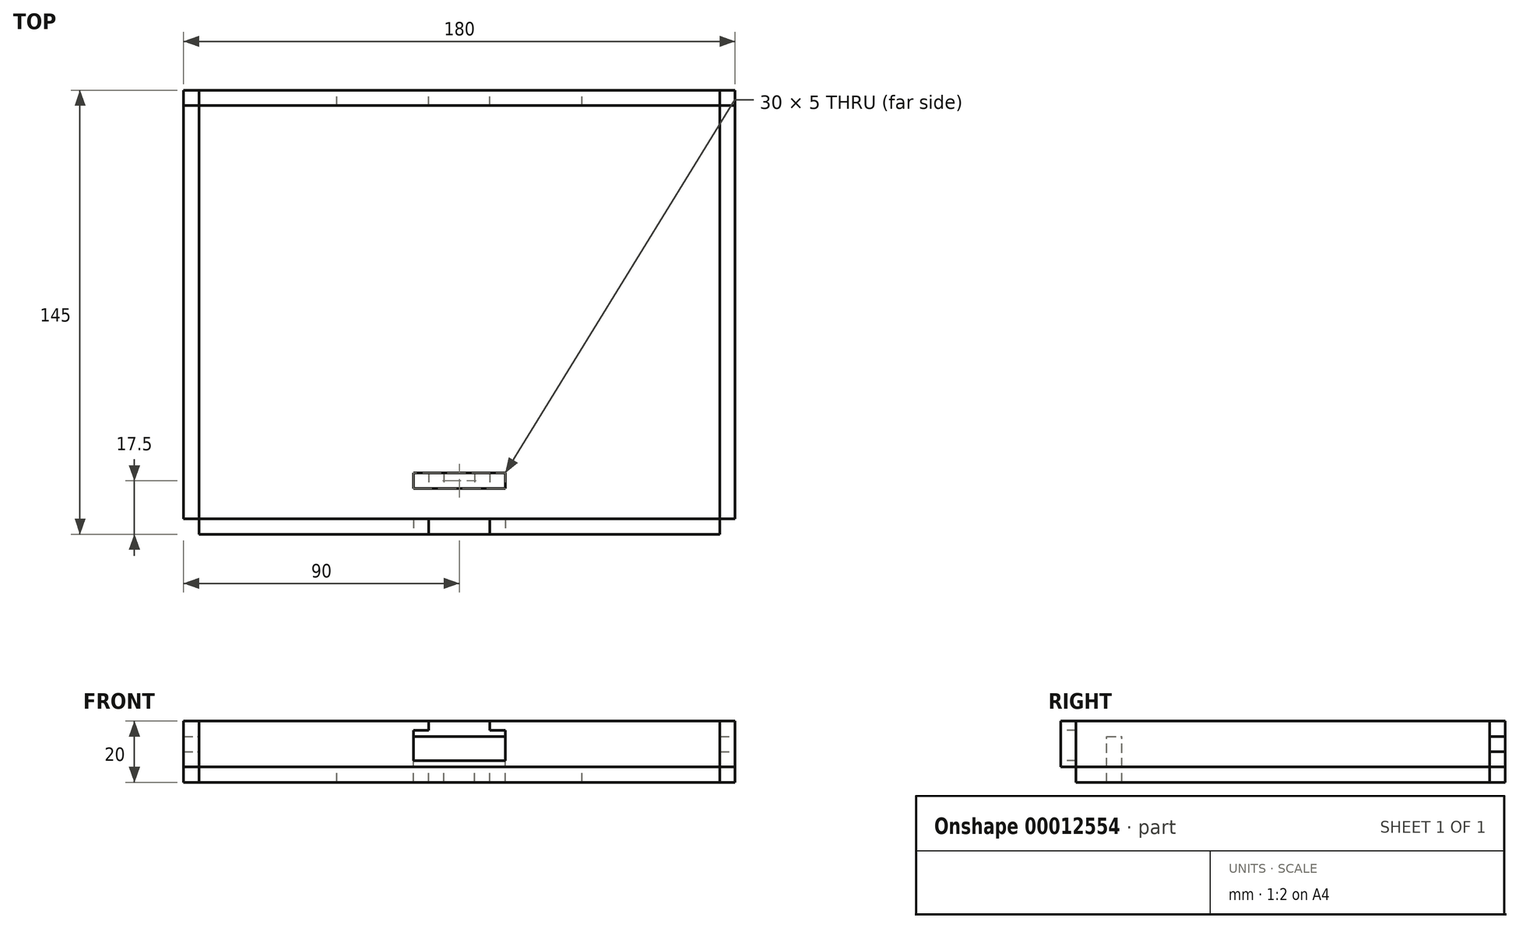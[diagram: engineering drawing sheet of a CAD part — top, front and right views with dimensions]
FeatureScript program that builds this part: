
annotation { "Feature Type Name" : "Feature", "Feature Type Description" : "" }
export const myFeature = defineFeature(function(context is Context, id is Id, definition is map)
    precondition{}
    {
        {
            var Q0;
            Q0=qCreatedBy(makeId("Top.planeOp"),FACE);
            var sketch = newSketch(context, id + "F0", { "sketchPlane" : qUnion([Q0])});
            skLineSegment(sketch, "E0.bottom", {"start": v(0, 0) * mm, "end": v(-180, 0) * mm});
            skLineSegment(sketch, "E0.top", {"start": v(0, 145) * mm, "end": v(-180, 145) * mm});
            skLineSegment(sketch, "E0.left", {"start": v(0, 0) * mm, "end": v(0, 145) * mm});
            skLineSegment(sketch, "E0.right", {"start": v(-180, 0) * mm, "end": v(-180, 145) * mm});
            skSolve(sketch);
        }
        {
            var Q0;
            Q0 = qSketchRegion(id + "F0", true);
            extrude(context, id + "F1", {"entities" : qUnion([Q0]), "depth" : 5 * mm});
        }
        {
            var Q0;
            Q0=makeQuery(id+"F1.opExtrude","SWEPT_FACE",FACE,{"disambiguationData":[OSD([sQuery(id+"F0.wireOp",EDGE,"E0.bottom")])]});
            var sketch = newSketch(context, id + "F2", { "sketchPlane" : qUnion([Q0])});
            skLineSegment(sketch, "E1.bottom", {"start": v(-180, 0) * mm, "end": v(0, 0) * mm});
            skLineSegment(sketch, "E1.top", {"start": v(-180, 20) * mm, "end": v(0, 20) * mm});
            skLineSegment(sketch, "E1.left", {"start": v(-180, 0) * mm, "end": v(-180, 20) * mm});
            skLineSegment(sketch, "E1.right", {"start": v(0, 0) * mm, "end": v(0, 20) * mm});
            skSolve(sketch);
        }
        {
            var Q0;
            Q0 = qSketchRegion(id + "F2", true);
            extrude(context, id + "F3", {"entities" : qUnion([Q0]), "oppositeDirection" : true, "depth" : 5 * mm});
        }
        {
            var Q0;
            Q0=makeQuery(id+"F1.opExtrude","SWEPT_FACE",FACE,{"disambiguationData":[OSD([sQuery(id+"F0.wireOp",EDGE,"E0.right")])]});
            var sketch = newSketch(context, id + "F4", { "sketchPlane" : qUnion([Q0])});
            skLineSegment(sketch, "E2.bottom", {"start": v(-145, 0) * mm, "end": v(0, 0) * mm});
            skLineSegment(sketch, "E2.top", {"start": v(-145, 20) * mm, "end": v(0, 20) * mm});
            skLineSegment(sketch, "E2.left", {"start": v(-145, 0) * mm, "end": v(-145, 20) * mm});
            skLineSegment(sketch, "E2.right", {"start": v(0, 0) * mm, "end": v(0, 20) * mm});
            skSolve(sketch);
        }
        {
            var Q0;
            Q0 = qSketchRegion(id + "F4", true);
            extrude(context, id + "F5", {"entities" : qUnion([Q0]), "oppositeDirection" : true, "depth" : 5 * mm});
        }
        {
            var Q0;
            Q0=makeQuery(id+"F1.opExtrude","SWEPT_FACE",FACE,{"disambiguationData":[OSD([sQuery(id+"F0.wireOp",EDGE,"E0.left")])]});
            var sketch = newSketch(context, id + "F6", { "sketchPlane" : qUnion([Q0])});
            skLineSegment(sketch, "E3.bottom", {"start": v(0, 0) * mm, "end": v(145, 0) * mm});
            skLineSegment(sketch, "E3.top", {"start": v(0, 20) * mm, "end": v(145, 20) * mm});
            skLineSegment(sketch, "E3.left", {"start": v(0, 0) * mm, "end": v(0, 20) * mm});
            skLineSegment(sketch, "E3.right", {"start": v(145, 0) * mm, "end": v(145, 20) * mm});
            skSolve(sketch);
        }
        {
            var Q0;
            Q0 = qSketchRegion(id + "F6", true);
            extrude(context, id + "F7", {"entities" : qUnion([Q0]), "oppositeDirection" : true, "depth" : 5 * mm});
        }
        {
            var Q0;
            Q0=makeQuery(id+"F5.opExtrude","CAP_FACE",FACE,{"disambiguationData":[OSD([sQuery(id+"F4.wireOp",EDGE,"E2.bottom"),sQuery(id+"F4.wireOp",EDGE,"E2.top"),sQuery(id+"F4.wireOp",EDGE,"E2.left"),sQuery(id+"F4.wireOp",EDGE,"E2.right")])],"isStart":true});
            var sketch = newSketch(context, id + "F8", { "sketchPlane" : qUnion([Q0])});
            skLineSegment(sketch, "E4.bottom", {"start": v(0, 5) * mm, "end": v(-5, 5) * mm});
            skLineSegment(sketch, "E4.top", {"start": v(0, 0) * mm, "end": v(-5, 0) * mm});
            skLineSegment(sketch, "E4.left", {"start": v(0, 5) * mm, "end": v(0, 0) * mm});
            skLineSegment(sketch, "E4.right", {"start": v(-5, 5) * mm, "end": v(-5, 0) * mm});
            skLineSegment(sketch, "E5.bottom", {"start": v(0, 10) * mm, "end": v(-5, 10) * mm});
            skLineSegment(sketch, "E5.top", {"start": v(0, 15) * mm, "end": v(-5, 15) * mm});
            skLineSegment(sketch, "E5.left", {"start": v(0, 10) * mm, "end": v(0, 15) * mm});
            skLineSegment(sketch, "E5.right", {"start": v(-5, 10) * mm, "end": v(-5, 15) * mm});
            skLineSegment(sketch, "E6.bottom", {"start": v(-30, 0) * mm, "end": v(-55, 0) * mm});
            skLineSegment(sketch, "E6.top", {"start": v(-30, 5) * mm, "end": v(-55, 5) * mm});
            skLineSegment(sketch, "E6.left", {"start": v(-30, 0) * mm, "end": v(-30, 5) * mm});
            skLineSegment(sketch, "E6.right", {"start": v(-55, 0) * mm, "end": v(-55, 5) * mm});
            skLineSegment(sketch, "E7.bottom", {"start": v(-85, 0) * mm, "end": v(-115, 0) * mm});
            skLineSegment(sketch, "E7.top", {"start": v(-85, 5) * mm, "end": v(-115, 5) * mm});
            skLineSegment(sketch, "E7.left", {"start": v(-85, 0) * mm, "end": v(-85, 5) * mm});
            skLineSegment(sketch, "E7.right", {"start": v(-115, 0) * mm, "end": v(-115, 5) * mm});
            skLineSegment(sketch, "E8.bottom", {"start": v(-145, 0) * mm, "end": v(-140, 0) * mm});
            skLineSegment(sketch, "E8.top", {"start": v(-145, 5) * mm, "end": v(-140, 5) * mm});
            skLineSegment(sketch, "E8.left", {"start": v(-145, 0) * mm, "end": v(-145, 5) * mm});
            skLineSegment(sketch, "E8.right", {"start": v(-140, 0) * mm, "end": v(-140, 5) * mm});
            skLineSegment(sketch, "E9.bottom", {"start": v(-145, 10) * mm, "end": v(-140, 10) * mm});
            skLineSegment(sketch, "E9.top", {"start": v(-145, 15) * mm, "end": v(-140, 15) * mm});
            skLineSegment(sketch, "E9.left", {"start": v(-145, 10) * mm, "end": v(-145, 15) * mm});
            skLineSegment(sketch, "E9.right", {"start": v(-140, 10) * mm, "end": v(-140, 15) * mm});
            skSolve(sketch);
        }
        {
            var Q0;
            Q0 = qSketchRegion(id + "F8", true);
            extrude(context, id + "F9", {"entities" : qUnion([Q0]), "operationType" : NewBodyOperationType.REMOVE, "oppositeDirection" : true, "depth" : 5 * mm});
        }
        {
            var Q0;
            Q0=makeQuery(id+"F1.opExtrude","CAP_FACE",FACE,{"disambiguationData":[OSD([sQuery(id+"F0.wireOp",EDGE,"E0.bottom"),sQuery(id+"F0.wireOp",EDGE,"E0.top"),sQuery(id+"F0.wireOp",EDGE,"E0.left"),sQuery(id+"F0.wireOp",EDGE,"E0.right")])],"isStart":false});
            var sketch = newSketch(context, id + "F10", { "sketchPlane" : qUnion([Q0])});
            skLineSegment(sketch, "E10.bottom", {"start": v(-180, 0) * mm, "end": v(-160, 0) * mm});
            skLineSegment(sketch, "E10.top", {"start": v(-180, 5) * mm, "end": v(-160, 5) * mm});
            skLineSegment(sketch, "E10.left", {"start": v(-180, 0) * mm, "end": v(-180, 5) * mm});
            skLineSegment(sketch, "E10.right", {"start": v(-160, 0) * mm, "end": v(-160, 5) * mm});
            skLineSegment(sketch, "E11.bottom", {"start": v(-130, 0) * mm, "end": v(-50, 0) * mm});
            skLineSegment(sketch, "E11.top", {"start": v(-130, 5) * mm, "end": v(-50, 5) * mm});
            skLineSegment(sketch, "E11.left", {"start": v(-130, 0) * mm, "end": v(-130, 5) * mm});
            skLineSegment(sketch, "E11.right", {"start": v(-50, 0) * mm, "end": v(-50, 5) * mm});
            skLineSegment(sketch, "E12.bottom", {"start": v(-20, 0) * mm, "end": v(0, 0) * mm});
            skLineSegment(sketch, "E12.top", {"start": v(-20, 5) * mm, "end": v(0, 5) * mm});
            skLineSegment(sketch, "E12.left", {"start": v(-20, 0) * mm, "end": v(-20, 5) * mm});
            skLineSegment(sketch, "E12.right", {"start": v(0, 0) * mm, "end": v(0, 5) * mm});
            skLineSegment(sketch, "E13.bottom", {"start": v(0, 0) * mm, "end": v(-5, 0) * mm});
            skLineSegment(sketch, "E13.top", {"start": v(0, 30) * mm, "end": v(-5, 30) * mm});
            skLineSegment(sketch, "E13.left", {"start": v(0, 0) * mm, "end": v(0, 30) * mm});
            skLineSegment(sketch, "E13.right", {"start": v(-5, 0) * mm, "end": v(-5, 30) * mm});
            skLineSegment(sketch, "E14.bottom", {"start": v(0, 55) * mm, "end": v(-5, 55) * mm});
            skLineSegment(sketch, "E14.top", {"start": v(0, 85) * mm, "end": v(-5, 85) * mm});
            skLineSegment(sketch, "E14.left", {"start": v(0, 55) * mm, "end": v(0, 85) * mm});
            skLineSegment(sketch, "E14.right", {"start": v(-5, 55) * mm, "end": v(-5, 85) * mm});
            skLineSegment(sketch, "E15.bottom", {"start": v(0, 145) * mm, "end": v(-5, 145) * mm});
            skLineSegment(sketch, "E15.top", {"start": v(0, 115) * mm, "end": v(-5, 115) * mm});
            skLineSegment(sketch, "E15.left", {"start": v(0, 145) * mm, "end": v(0, 115) * mm});
            skLineSegment(sketch, "E15.right", {"start": v(-5, 145) * mm, "end": v(-5, 115) * mm});
            skLineSegment(sketch, "E16.bottom", {"start": v(-180, 0) * mm, "end": v(-175, 0) * mm});
            skLineSegment(sketch, "E16.top", {"start": v(-180, 30) * mm, "end": v(-175, 30) * mm});
            skLineSegment(sketch, "E16.left", {"start": v(-180, 0) * mm, "end": v(-180, 30) * mm});
            skLineSegment(sketch, "E16.right", {"start": v(-175, 0) * mm, "end": v(-175, 30) * mm});
            skLineSegment(sketch, "E17.bottom", {"start": v(-180, 55) * mm, "end": v(-175, 55) * mm});
            skLineSegment(sketch, "E17.top", {"start": v(-180, 85) * mm, "end": v(-175, 85) * mm});
            skLineSegment(sketch, "E17.left", {"start": v(-180, 55) * mm, "end": v(-180, 85) * mm});
            skLineSegment(sketch, "E17.right", {"start": v(-175, 55) * mm, "end": v(-175, 85) * mm});
            skLineSegment(sketch, "E18.bottom", {"start": v(-180, 115) * mm, "end": v(-175, 115) * mm});
            skLineSegment(sketch, "E18.right", {"start": v(-175, 115) * mm, "end": v(-175, 145) * mm});
            skLineSegment(sketch, "E19.bottom", {"start": v(-50, 145) * mm, "end": v(0, 145) * mm});
            skLineSegment(sketch, "E19.top", {"start": v(-50, 140) * mm, "end": v(0, 140) * mm});
            skLineSegment(sketch, "E19.left", {"start": v(-50, 145) * mm, "end": v(-50, 140) * mm});
            skLineSegment(sketch, "E19.right", {"start": v(0, 145) * mm, "end": v(0, 140) * mm});
            skLineSegment(sketch, "E20.bottom", {"start": v(-80, 145) * mm, "end": v(-100, 145) * mm});
            skLineSegment(sketch, "E20.top", {"start": v(-80, 140) * mm, "end": v(-100, 140) * mm});
            skLineSegment(sketch, "E20.left", {"start": v(-80, 145) * mm, "end": v(-80, 140) * mm});
            skLineSegment(sketch, "E20.right", {"start": v(-100, 145) * mm, "end": v(-100, 140) * mm});
            skLineSegment(sketch, "E21.bottom", {"start": v(-130, 140) * mm, "end": v(-175, 140) * mm});
            skLineSegment(sketch, "E21.top", {"start": v(-130, 145) * mm, "end": v(-175, 145) * mm});
            skLineSegment(sketch, "E21.left", {"start": v(-130, 140) * mm, "end": v(-130, 145) * mm});
            skLineSegment(sketch, "E21.right", {"start": v(-175, 140) * mm, "end": v(-175, 145) * mm});
            skLineSegment(sketch, "E22.top", {"start": v(-180, 145) * mm, "end": v(-175, 145) * mm});
            skLineSegment(sketch, "E22.left", {"start": v(-180, 115) * mm, "end": v(-180, 145) * mm});
            skLineSegment(sketch, "E23.bottom", {"start": v(-100, 15) * mm, "end": v(-95, 15) * mm});
            skLineSegment(sketch, "E23.top", {"start": v(-100, 20) * mm, "end": v(-95, 20) * mm});
            skLineSegment(sketch, "E23.left", {"start": v(-100, 15) * mm, "end": v(-100, 20) * mm});
            skLineSegment(sketch, "E23.right", {"start": v(-95, 15) * mm, "end": v(-95, 20) * mm});
            skLineSegment(sketch, "E24.bottom", {"start": v(-85, 15) * mm, "end": v(-80, 15) * mm});
            skLineSegment(sketch, "E24.top", {"start": v(-85, 20) * mm, "end": v(-80, 20) * mm});
            skLineSegment(sketch, "E24.left", {"start": v(-85, 15) * mm, "end": v(-85, 20) * mm});
            skLineSegment(sketch, "E24.right", {"start": v(-80, 15) * mm, "end": v(-80, 20) * mm});
            skSolve(sketch);
        }
        {
            var Q0;
            Q0 = qSketchRegion(id + "F10", true);
            extrude(context, id + "F11", {"entities" : qUnion([Q0]), "operationType" : NewBodyOperationType.REMOVE, "oppositeDirection" : true, "depth" : 5 * mm});
        }
        {
            var Q0;
            Q0=makeQuery(id+"F3.opExtrude","CAP_FACE",FACE,{"disambiguationData":[OSD([sQuery(id+"F2.wireOp",EDGE,"E1.bottom"),sQuery(id+"F2.wireOp",EDGE,"E1.top"),sQuery(id+"F2.wireOp",EDGE,"E1.left"),sQuery(id+"F2.wireOp",EDGE,"E1.right")])],"isStart":true});
            var sketch = newSketch(context, id + "F12", { "sketchPlane" : qUnion([Q0])});
            skLineSegment(sketch, "E25.bottom", {"start": v(-180, 5) * mm, "end": v(-175, 5) * mm});
            skLineSegment(sketch, "E25.top", {"start": v(-180, 10) * mm, "end": v(-175, 10) * mm});
            skLineSegment(sketch, "E25.left", {"start": v(-180, 5) * mm, "end": v(-180, 10) * mm});
            skLineSegment(sketch, "E25.right", {"start": v(-175, 5) * mm, "end": v(-175, 10) * mm});
            skLineSegment(sketch, "E26.bottom", {"start": v(-180, 15) * mm, "end": v(-175, 15) * mm});
            skLineSegment(sketch, "E26.top", {"start": v(-180, 20) * mm, "end": v(-175, 20) * mm});
            skLineSegment(sketch, "E26.left", {"start": v(-180, 15) * mm, "end": v(-180, 20) * mm});
            skLineSegment(sketch, "E26.right", {"start": v(-175, 15) * mm, "end": v(-175, 20) * mm});
            skLineSegment(sketch, "E27.bottom", {"start": v(0, 20) * mm, "end": v(-5, 20) * mm});
            skLineSegment(sketch, "E27.top", {"start": v(0, 15) * mm, "end": v(-5, 15) * mm});
            skLineSegment(sketch, "E27.left", {"start": v(0, 20) * mm, "end": v(0, 15) * mm});
            skLineSegment(sketch, "E27.right", {"start": v(-5, 20) * mm, "end": v(-5, 15) * mm});
            skLineSegment(sketch, "E28.bottom", {"start": v(0, 10) * mm, "end": v(-5, 10) * mm});
            skLineSegment(sketch, "E28.top", {"start": v(0, 5) * mm, "end": v(-5, 5) * mm});
            skLineSegment(sketch, "E28.left", {"start": v(0, 10) * mm, "end": v(0, 5) * mm});
            skLineSegment(sketch, "E28.right", {"start": v(-5, 10) * mm, "end": v(-5, 5) * mm});
            skLineSegment(sketch, "E29.bottom", {"start": v(-130, 5) * mm, "end": v(-160, 5) * mm});
            skLineSegment(sketch, "E29.top", {"start": v(-130, 0) * mm, "end": v(-160, 0) * mm});
            skLineSegment(sketch, "E29.left", {"start": v(-130, 5) * mm, "end": v(-130, 0) * mm});
            skLineSegment(sketch, "E29.right", {"start": v(-160, 5) * mm, "end": v(-160, 0) * mm});
            skLineSegment(sketch, "E30.bottom", {"start": v(-50, 5) * mm, "end": v(-20, 5) * mm});
            skLineSegment(sketch, "E30.top", {"start": v(-50, 0) * mm, "end": v(-20, 0) * mm});
            skLineSegment(sketch, "E30.left", {"start": v(-50, 5) * mm, "end": v(-50, 0) * mm});
            skLineSegment(sketch, "E30.right", {"start": v(-20, 5) * mm, "end": v(-20, 0) * mm});
            skLineSegment(sketch, "E31.bottom", {"start": v(-105, 7) * mm, "end": v(-75, 7) * mm});
            skLineSegment(sketch, "E31.top", {"start": v(-105, 17) * mm, "end": v(-75, 17) * mm});
            skLineSegment(sketch, "E31.left", {"start": v(-105, 7) * mm, "end": v(-105, 17) * mm});
            skLineSegment(sketch, "E31.right", {"start": v(-75, 7) * mm, "end": v(-75, 17) * mm});
            skLineSegment(sketch, "E32.bottom", {"start": v(-100, 17) * mm, "end": v(-80, 17) * mm});
            skLineSegment(sketch, "E32.top", {"start": v(-100, 20) * mm, "end": v(-80, 20) * mm});
            skLineSegment(sketch, "E32.left", {"start": v(-100, 17) * mm, "end": v(-100, 20) * mm});
            skLineSegment(sketch, "E32.right", {"start": v(-80, 17) * mm, "end": v(-80, 20) * mm});
            skSolve(sketch);
        }
        {
            var Q0;
            Q0 = qSketchRegion(id + "F12", true);
            extrude(context, id + "F13", {"entities" : qUnion([Q0]), "operationType" : NewBodyOperationType.REMOVE, "oppositeDirection" : true, "depth" : 5 * mm});
        }
        {
            var Q0;
            Q0=makeQuery(id+"F7.opExtrude","CAP_FACE",FACE,{"disambiguationData":[OSD([sQuery(id+"F6.wireOp",EDGE,"E3.bottom"),sQuery(id+"F6.wireOp",EDGE,"E3.top"),sQuery(id+"F6.wireOp",EDGE,"E3.left"),sQuery(id+"F6.wireOp",EDGE,"E3.right")])],"isStart":true});
            var sketch = newSketch(context, id + "F14", { "sketchPlane" : qUnion([Q0])});
            skLineSegment(sketch, "E33.bottom", {"start": v(0, 0) * mm, "end": v(5, 0) * mm});
            skLineSegment(sketch, "E33.top", {"start": v(0, 5) * mm, "end": v(5, 5) * mm});
            skLineSegment(sketch, "E33.left", {"start": v(0, 0) * mm, "end": v(0, 5) * mm});
            skLineSegment(sketch, "E33.right", {"start": v(5, 0) * mm, "end": v(5, 5) * mm});
            skLineSegment(sketch, "E34.bottom", {"start": v(0, 10) * mm, "end": v(5, 10) * mm});
            skLineSegment(sketch, "E34.top", {"start": v(0, 15) * mm, "end": v(5, 15) * mm});
            skLineSegment(sketch, "E34.left", {"start": v(0, 10) * mm, "end": v(0, 15) * mm});
            skLineSegment(sketch, "E34.right", {"start": v(5, 10) * mm, "end": v(5, 15) * mm});
            skLineSegment(sketch, "E35.bottom", {"start": v(30, 5) * mm, "end": v(55, 5) * mm});
            skLineSegment(sketch, "E35.top", {"start": v(30, 0) * mm, "end": v(55, 0) * mm});
            skLineSegment(sketch, "E35.left", {"start": v(30, 5) * mm, "end": v(30, 0) * mm});
            skLineSegment(sketch, "E35.right", {"start": v(55, 5) * mm, "end": v(55, 0) * mm});
            skLineSegment(sketch, "E36.bottom", {"start": v(85, 5) * mm, "end": v(115, 5) * mm});
            skLineSegment(sketch, "E36.top", {"start": v(85, 0) * mm, "end": v(115, 0) * mm});
            skLineSegment(sketch, "E36.left", {"start": v(85, 5) * mm, "end": v(85, 0) * mm});
            skLineSegment(sketch, "E36.right", {"start": v(115, 5) * mm, "end": v(115, 0) * mm});
            skLineSegment(sketch, "E37.bottom", {"start": v(145, 0) * mm, "end": v(140, 0) * mm});
            skLineSegment(sketch, "E37.top", {"start": v(145, 5) * mm, "end": v(140, 5) * mm});
            skLineSegment(sketch, "E37.left", {"start": v(145, 0) * mm, "end": v(145, 5) * mm});
            skLineSegment(sketch, "E37.right", {"start": v(140, 0) * mm, "end": v(140, 5) * mm});
            skLineSegment(sketch, "E38.bottom", {"start": v(145, 10) * mm, "end": v(140, 10) * mm});
            skLineSegment(sketch, "E38.top", {"start": v(145, 15) * mm, "end": v(140, 15) * mm});
            skLineSegment(sketch, "E38.left", {"start": v(145, 10) * mm, "end": v(145, 15) * mm});
            skLineSegment(sketch, "E38.right", {"start": v(140, 10) * mm, "end": v(140, 15) * mm});
            skSolve(sketch);
        }
        {
            var Q0;
            Q0 = qSketchRegion(id + "F14", true);
            extrude(context, id + "F15", {"entities" : qUnion([Q0]), "operationType" : NewBodyOperationType.REMOVE, "oppositeDirection" : true, "depth" : 5 * mm});
        }
        {
            var Q0;
            Q0=makeQuery(id+"F1.opExtrude","SWEPT_FACE",FACE,{"disambiguationData":[OSD([sQuery(id+"F0.wireOp",EDGE,"E0.top")])]});
            var sketch = newSketch(context, id + "F16", { "sketchPlane" : qUnion([Q0])});
            skLineSegment(sketch, "E39.bottom", {"start": v(0, 0) * mm, "end": v(180, 0) * mm});
            skLineSegment(sketch, "E39.top", {"start": v(0, 20) * mm, "end": v(180, 20) * mm});
            skLineSegment(sketch, "E39.left", {"start": v(0, 0) * mm, "end": v(0, 20) * mm});
            skLineSegment(sketch, "E39.right", {"start": v(180, 0) * mm, "end": v(180, 20) * mm});
            skSolve(sketch);
        }
        {
            var Q0;
            Q0 = qSketchRegion(id + "F16", true);
            extrude(context, id + "F17", {"entities" : qUnion([Q0]), "oppositeDirection" : true, "depth" : 5 * mm});
        }
        {
            var Q0;
            Q0=makeQuery(id+"F17.opExtrude","CAP_FACE",FACE,{"disambiguationData":[OSD([sQuery(id+"F16.wireOp",EDGE,"E39.bottom"),sQuery(id+"F16.wireOp",EDGE,"E39.top"),sQuery(id+"F16.wireOp",EDGE,"E39.left"),sQuery(id+"F16.wireOp",EDGE,"E39.right")])],"isStart":true});
            var sketch = newSketch(context, id + "F18", { "sketchPlane" : qUnion([Q0])});
            skLineSegment(sketch, "E40.bottom", {"start": v(5, 5) * mm, "end": v(0, 5) * mm});
            skLineSegment(sketch, "E40.top", {"start": v(5, 10) * mm, "end": v(0, 10) * mm});
            skLineSegment(sketch, "E40.left", {"start": v(5, 5) * mm, "end": v(5, 10) * mm});
            skLineSegment(sketch, "E40.right", {"start": v(0, 5) * mm, "end": v(0, 10) * mm});
            skLineSegment(sketch, "E41.bottom", {"start": v(5, 15) * mm, "end": v(0, 15) * mm});
            skLineSegment(sketch, "E41.top", {"start": v(5, 20) * mm, "end": v(0, 20) * mm});
            skLineSegment(sketch, "E41.left", {"start": v(5, 15) * mm, "end": v(5, 20) * mm});
            skLineSegment(sketch, "E41.right", {"start": v(0, 15) * mm, "end": v(0, 20) * mm});
            skLineSegment(sketch, "E42.bottom", {"start": v(180, 20) * mm, "end": v(175, 20) * mm});
            skLineSegment(sketch, "E42.top", {"start": v(180, 15) * mm, "end": v(175, 15) * mm});
            skLineSegment(sketch, "E42.left", {"start": v(180, 20) * mm, "end": v(180, 15) * mm});
            skLineSegment(sketch, "E42.right", {"start": v(175, 20) * mm, "end": v(175, 15) * mm});
            skLineSegment(sketch, "E43.bottom", {"start": v(180, 10) * mm, "end": v(175, 10) * mm});
            skLineSegment(sketch, "E43.top", {"start": v(180, 5) * mm, "end": v(175, 5) * mm});
            skLineSegment(sketch, "E43.left", {"start": v(180, 10) * mm, "end": v(180, 5) * mm});
            skLineSegment(sketch, "E43.right", {"start": v(175, 10) * mm, "end": v(175, 5) * mm});
            skLineSegment(sketch, "E44.bottom", {"start": v(50, 0) * mm, "end": v(80, 0) * mm});
            skLineSegment(sketch, "E44.top", {"start": v(50, 5) * mm, "end": v(80, 5) * mm});
            skLineSegment(sketch, "E44.left", {"start": v(50, 0) * mm, "end": v(50, 5) * mm});
            skLineSegment(sketch, "E44.right", {"start": v(80, 0) * mm, "end": v(80, 5) * mm});
            skLineSegment(sketch, "E45.bottom", {"start": v(100, 0) * mm, "end": v(130, 0) * mm});
            skLineSegment(sketch, "E45.top", {"start": v(100, 5) * mm, "end": v(130, 5) * mm});
            skLineSegment(sketch, "E45.left", {"start": v(100, 0) * mm, "end": v(100, 5) * mm});
            skLineSegment(sketch, "E45.right", {"start": v(130, 0) * mm, "end": v(130, 5) * mm});
            skSolve(sketch);
        }
        {
            var Q0;
            Q0 = qSketchRegion(id + "F18", true);
            extrude(context, id + "F19", {"entities" : qUnion([Q0]), "operationType" : NewBodyOperationType.REMOVE, "oppositeDirection" : true, "depth" : 5 * mm});
        }
        {
            var Q0;
            Q0=makeQuery(id+"F3.opExtrude","CAP_FACE",FACE,{"disambiguationData":[OSD([sQuery(id+"F2.wireOp",EDGE,"E1.bottom"),sQuery(id+"F2.wireOp",EDGE,"E1.top"),sQuery(id+"F2.wireOp",EDGE,"E1.left"),sQuery(id+"F2.wireOp",EDGE,"E1.right")])],"isStart":true});
            var sketch = newSketch(context, id + "F20", { "sketchPlane" : qUnion([Q0])});
            skLineSegment(sketch, "E46.bottom", {"start": v(0, 0) * mm, "end": v(-180, 0) * mm});
            skLineSegment(sketch, "E46.top", {"start": v(0, 3) * mm, "end": v(-180, 3) * mm});
            skLineSegment(sketch, "E46.left", {"start": v(0, 0) * mm, "end": v(0, 3) * mm});
            skLineSegment(sketch, "E46.right", {"start": v(-180, 0) * mm, "end": v(-180, 3) * mm});
            skSolve(sketch);
        }
        {
            var Q0;
            Q0 = qSketchRegion(id + "F20", true);
            extrude(context, id + "F21", {"entities" : qUnion([Q0]), "operationType" : NewBodyOperationType.REMOVE, "oppositeDirection" : true, "depth" : 5 * mm});
        }
        {
            var Q0;
            Q0=makeQuery(id+"F11.boolean.opBoolean","COPY",FACE,{"derivedFrom":makeQuery(id+"F11.opExtrude","SWEPT_FACE",FACE,{"disambiguationData":[OSD([sQuery(id+"F10.wireOp",EDGE,"E23.top")])]})});
            var sketch = newSketch(context, id + "F22", { "sketchPlane" : qUnion([Q0])});
            skLineSegment(sketch, "E47.bottom", {"start": v(-105, 0) * mm, "end": v(-75, 0) * mm});
            skLineSegment(sketch, "E47.top", {"start": v(-105, 15) * mm, "end": v(-75, 15) * mm});
            skLineSegment(sketch, "E47.left", {"start": v(-105, 0) * mm, "end": v(-105, 15) * mm});
            skLineSegment(sketch, "E47.right", {"start": v(-75, 0) * mm, "end": v(-75, 15) * mm});
            skSolve(sketch);
        }
        {
            var Q0;
            Q0 = qSketchRegion(id + "F22", true);
            extrude(context, id + "F23", {"entities" : qUnion([Q0]), "depth" : 5 * mm});
        }
        {
            var Q0;
            Q0=makeQuery(id+"F23.opExtrude","CAP_FACE",FACE,{"disambiguationData":[OSD([sQuery(id+"F22.wireOp",EDGE,"E47.bottom"),sQuery(id+"F22.wireOp",EDGE,"E47.top"),sQuery(id+"F22.wireOp",EDGE,"E47.left"),sQuery(id+"F22.wireOp",EDGE,"E47.right")])],"isStart":false});
            var sketch = newSketch(context, id + "F24", { "sketchPlane" : qUnion([Q0])});
            skLineSegment(sketch, "E48.bottom", {"start": v(-105, 0) * mm, "end": v(-100, 0) * mm});
            skLineSegment(sketch, "E48.top", {"start": v(-105, 5) * mm, "end": v(-100, 5) * mm});
            skLineSegment(sketch, "E48.left", {"start": v(-105, 0) * mm, "end": v(-105, 5) * mm});
            skLineSegment(sketch, "E48.right", {"start": v(-100, 0) * mm, "end": v(-100, 5) * mm});
            skLineSegment(sketch, "E49.bottom", {"start": v(-95, 0) * mm, "end": v(-85, 0) * mm});
            skLineSegment(sketch, "E49.top", {"start": v(-95, 5) * mm, "end": v(-85, 5) * mm});
            skLineSegment(sketch, "E49.left", {"start": v(-95, 0) * mm, "end": v(-95, 5) * mm});
            skLineSegment(sketch, "E49.right", {"start": v(-85, 0) * mm, "end": v(-85, 5) * mm});
            skLineSegment(sketch, "E50.bottom", {"start": v(-75, 0) * mm, "end": v(-80, 0) * mm});
            skLineSegment(sketch, "E50.top", {"start": v(-75, 5) * mm, "end": v(-80, 5) * mm});
            skLineSegment(sketch, "E50.left", {"start": v(-75, 0) * mm, "end": v(-75, 5) * mm});
            skLineSegment(sketch, "E50.right", {"start": v(-80, 0) * mm, "end": v(-80, 5) * mm});
            skSolve(sketch);
        }
        {
            var Q0;
            Q0 = qSketchRegion(id + "F24", true);
            extrude(context, id + "F25", {"entities" : qUnion([Q0]), "operationType" : NewBodyOperationType.REMOVE, "oppositeDirection" : true, "depth" : 5 * mm});
        }
    });
